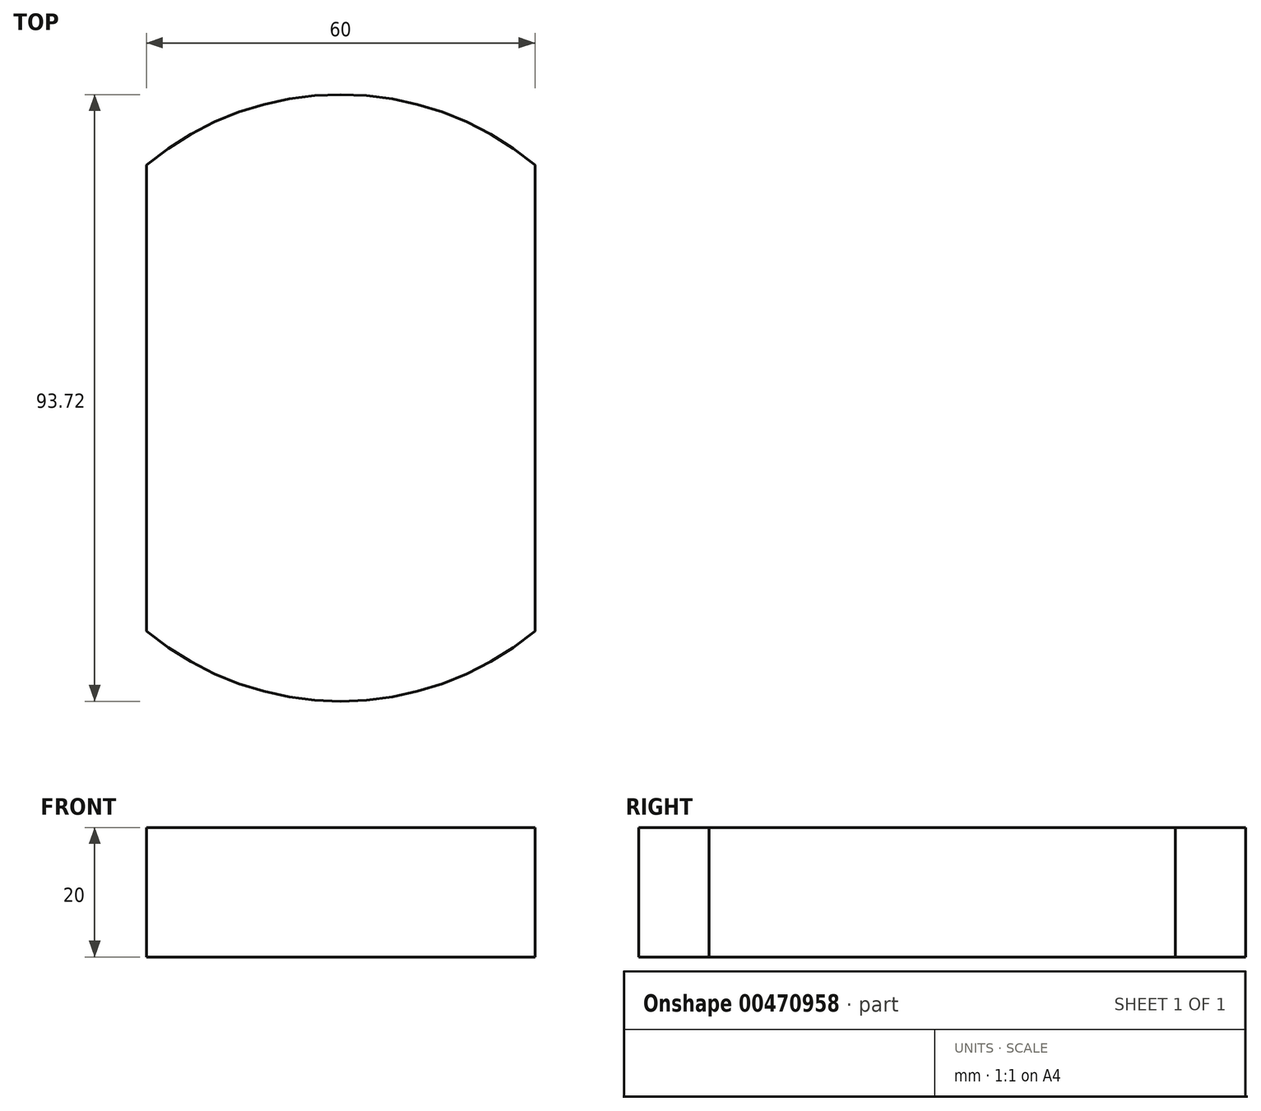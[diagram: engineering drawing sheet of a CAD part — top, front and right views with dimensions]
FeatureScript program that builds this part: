
annotation { "Feature Type Name" : "Feature", "Feature Type Description" : "" }
export const myFeature = defineFeature(function(context is Context, id is Id, definition is map)
    precondition{}
    {
        {
            var Q0;
            Q0=qCreatedBy(makeId("Top.planeOp"),FACE);
            var sketch = newSketch(context, id + "F0", { "sketchPlane" : qUnion([Q0])});
            skLineSegment(sketch, "E0", {"start": v(30, 36) * mm, "end": v(30, -36) * mm});
            skLineSegment(sketch, "E1", {"start": v(-30, -36) * mm, "end": v(-30, 36) * mm});
            skPoint(sketch, "E2", {"position": v(-30, 0) * mm});
            skPoint(sketch, "E3", {"position": v(30, 0) * mm});
            skArc(sketch, "E4", {"start": v(-30, -36) * mm, "mid": v(0, -46.86) * mm, "end": v(30, -36) * mm});
            skArc(sketch, "E5.trimOffspring", {"start": v(30, 36) * mm, "mid": v(0, 46.86) * mm, "end": v(-30, 36) * mm});
            skSolve(sketch);
        }
        {
            var Q0;
            Q0=makeQuery(id+"F0.imprint","IMPRINT",FACE,{"disambiguationData":[TD([[makeQuery(id+"F0.imprint","IMPRINT",EDGE,{"derivedFrom":sQuery(id+"F0.wireOp",EDGE,"E0")}),-1.0]])]});
            extrude(context, id + "F1", {"entities" : qUnion([Q0]), "depth" : 20 * mm});
        }
    });
